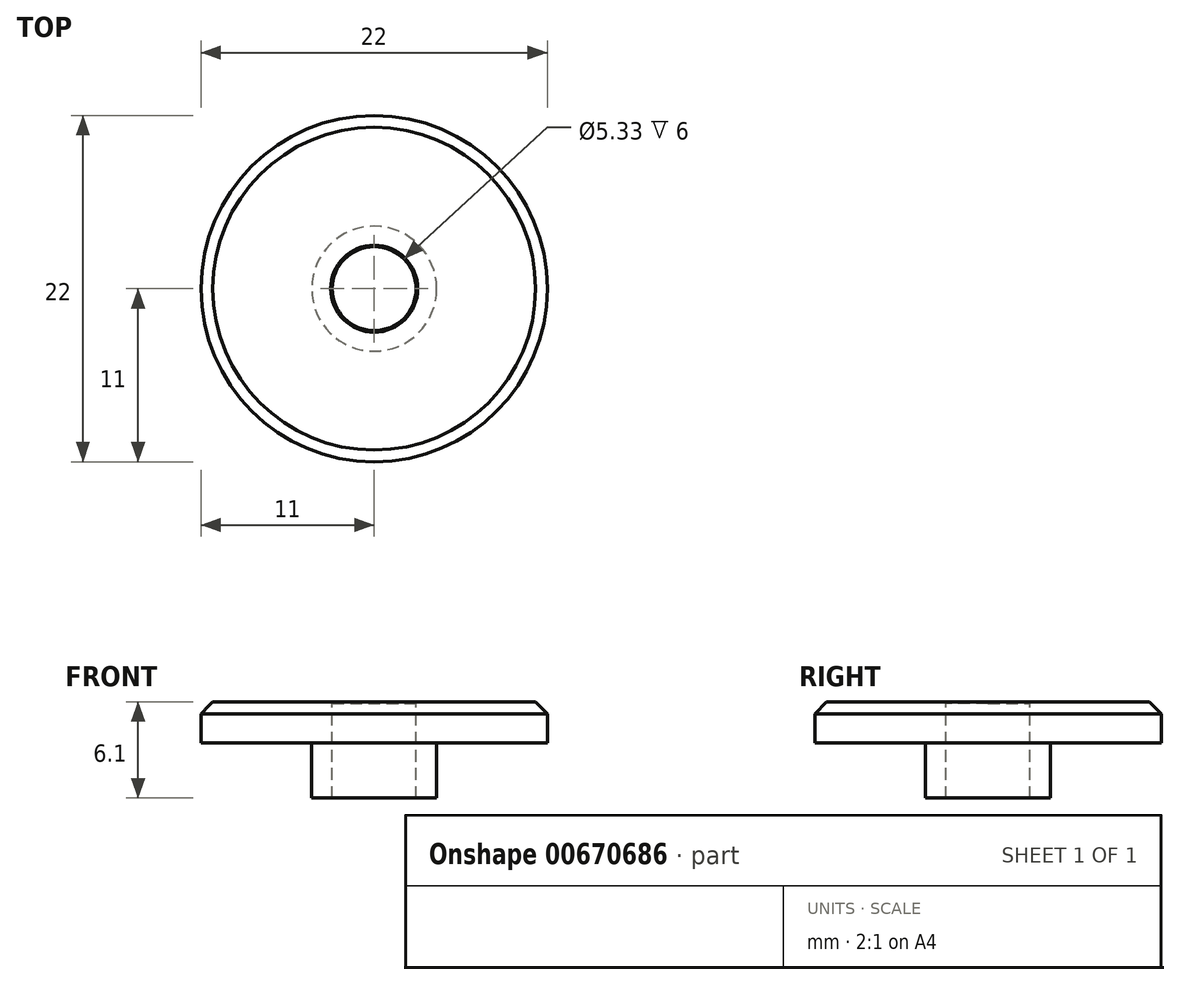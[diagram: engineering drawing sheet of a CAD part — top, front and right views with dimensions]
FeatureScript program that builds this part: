
annotation { "Feature Type Name" : "Feature", "Feature Type Description" : "" }
export const myFeature = defineFeature(function(context is Context, id is Id, definition is map)
    precondition{}
    {
        {
            var Q0;
            Q0=qCreatedBy(makeId("Front.planeOp"),FACE);
            var sketch = newSketch(context, id + "F0", { "sketchPlane" : qUnion([Q0])});
            skLineSegment(sketch, "E0.left", {"start": v(-11, 0) * mm, "end": v(-11, 2.6) * mm});
            skLineSegment(sketch, "E1.left", {"start": v(-3.97, 0) * mm, "end": v(-3.97, -3.5) * mm});
            skLineSegment(sketch, "E2", {"start": v(-11, 2.6) * mm, "end": v(-2.66, 2.6) * mm});
            skLineSegment(sketch, "E3", {"start": v(-2.66, 2.6) * mm, "end": v(-2.66, -3.5) * mm});
            skLineSegment(sketch, "E4", {"start": v(-2.66, -3.5) * mm, "end": v(-3.97, -3.5) * mm});
            skLineSegment(sketch, "E5", {"start": v(0, 2.6) * mm, "end": v(0, -3.5) * mm});
            skLineSegment(sketch, "E6", {"start": v(-11, 0) * mm, "end": v(-3.97, 0) * mm});
            skLineSegment(sketch, "E7", {"start": v(-3.97, -3.5) * mm, "end": v(0, -3.5) * mm});
            skSolve(sketch);
        }
        {
            var Q0;
            Q0=makeQuery(id+"F0.imprint","IMPRINT",FACE,{"disambiguationData":[TD([[makeQuery(id+"F0.imprint","IMPRINT",EDGE,{"derivedFrom":sQuery(id+"F0.wireOp",EDGE,"E0.left")}),-1.0]])]});
            var Q1;
            Q1=sQuery(id+"F0.wireOp",EDGE,"E5");
            revolve(context, id + "F1", {"entities" : qUnion([Q0]), "axis" : qUnion([Q1]), "revolveType" : RevolveType.FULL});
        }
        {
            var Q0;
            Q0=makeQuery(id+"F1.opRevolve","SWEPT_EDGE",EDGE,{"disambiguationData":[OSD([sQuery(id+"F0.wireOp",EDGE,"E0.left"),sQuery(id+"F0.wireOp",EDGE,"E2")])]});
            chamfer(context, id + "F2", {"entities" : qUnion([Q0]), "width" : .75 * mm, "tangentPropagation" : true});
        }
        {
            var Q0;
            Q0=makeQuery(id+"F1.opRevolve","SWEPT_EDGE",EDGE,{"disambiguationData":[OSD([sQuery(id+"F0.wireOp",EDGE,"E2"),sQuery(id+"F0.wireOp",EDGE,"E3")])]});
            chamfer(context, id + "F3", {"entities" : qUnion([Q0]), "width" : .1 * mm, "tangentPropagation" : true});
        }
    });
